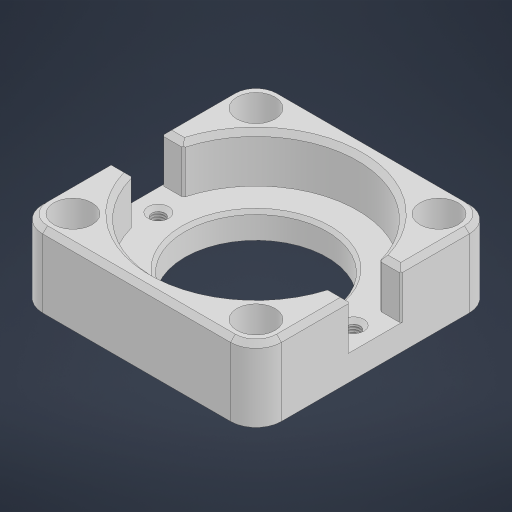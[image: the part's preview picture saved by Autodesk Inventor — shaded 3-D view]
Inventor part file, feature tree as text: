
AUTODESK INVENTOR PART (.ipt)
format: ipt  version: 2024.3 (Build 283343000, 343)  size: 291,328 bytes
history: native  units: mm
features: chamfer x3, sketch x2, extrude x2, hole x2, fillet x1
ambient origin geometry x8: Origin, YZ Plane, XZ Plane, XY Plane, X Axis, Y Axis, Z Axis, Center Point
bodies: Solid1 (feature_tree)
feature tree (10):
  sketch  "Sketch1"  dims[d0=75.0mm d1=44.65mm]
  extrude  "Extrusion1"  Depth=75.0mm
  extrude  "Extrusion2"  Depth=8.0mm
  hole  "Hole1"  [1 undecoded]
  hole  "Hole2"  [1 undecoded]
  fillet  "Fillet1"  Radius=16.0mm
  chamfer  "Chamfer1"  Distance=15.0mm
  chamfer  "Chamfer2"  Distance=8.0mm
  chamfer  "Chamfer3"  Distance=1.5mm Angle=45.0deg
  sketch  "Sketch2"  dims[d2=63.75mm d3=57.5mm d4=61.33mm d5=23.0mm d6=0.0mm d7=16.0mm d8=15.0mm d9=0.0mm d10=6.5mm d11=10.0mm d12=12.0mm d13=12.0mm d14=90.0deg d15=8.0mm d16=20.594885mm d17=4.134mm d18=10.0mm d19=6.5mm d20=12.0mm d21=90.0deg d22=8.0mm d23=20.594885mm d24=8.0mm d25=1.5mm d26=2.0mm d27=45.0deg d28=1.0mm d29=2.0mm d30=45.0deg d31=0.5mm d32=2.0mm d33=45.0deg]
note: 2 required parameter values undecoded (feature->parameter linkage not recoverable at this tier; creation-order binding heuristic only, values carry confidence <= 0.55)
